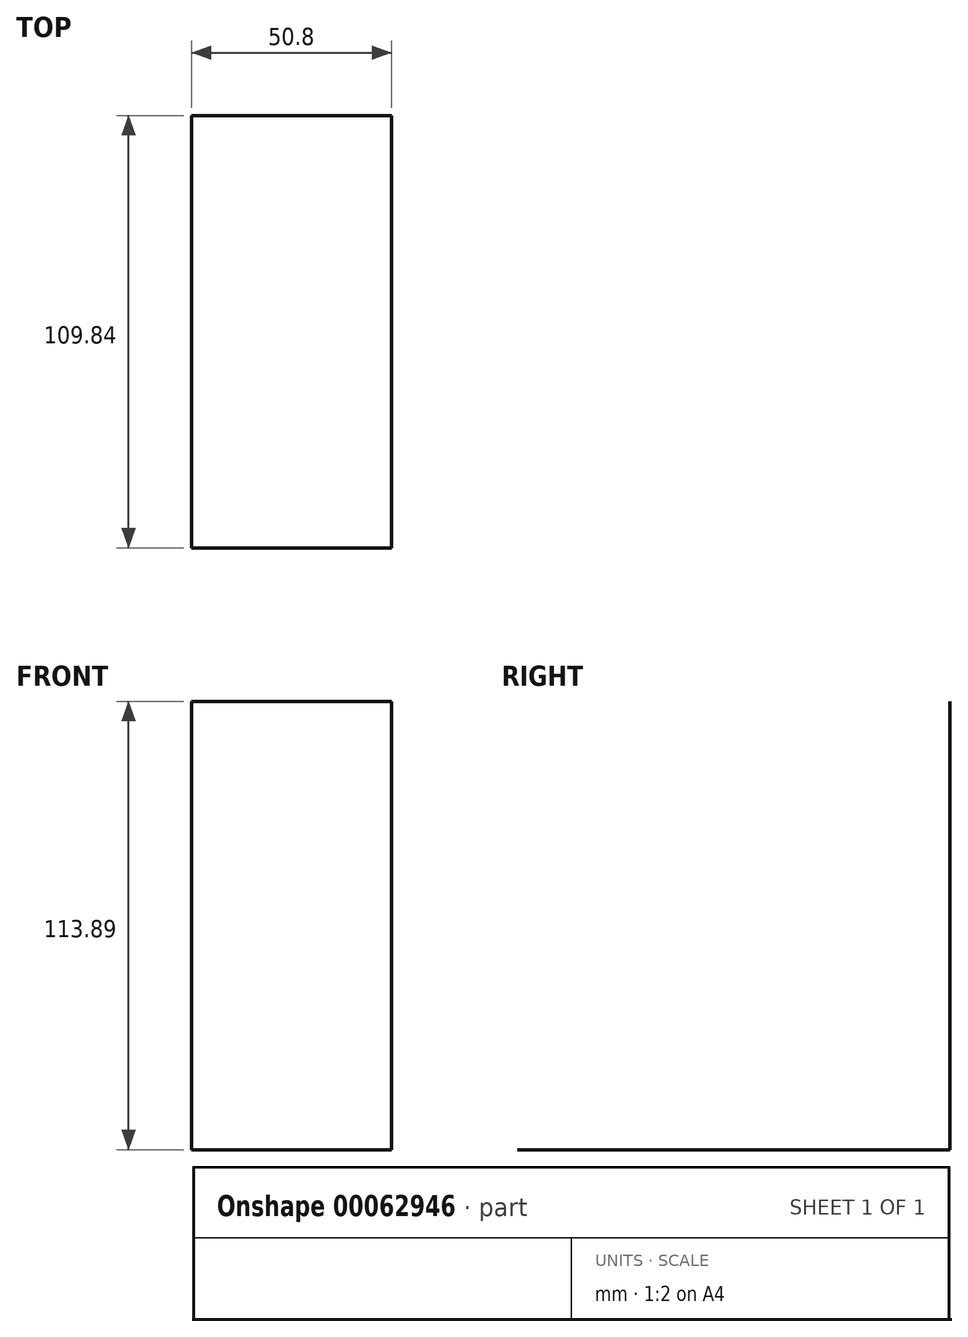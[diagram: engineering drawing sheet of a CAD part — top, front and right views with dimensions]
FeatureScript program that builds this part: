
annotation { "Feature Type Name" : "Feature", "Feature Type Description" : "" }
export const myFeature = defineFeature(function(context is Context, id is Id, definition is map)
    precondition{}
    {
        {
            var Q0;
            Q0=qCreatedBy(makeId("Right.planeOp"),FACE);
            var sketch = newSketch(context, id + "F0", { "sketchPlane" : qUnion([Q0])});
            skLineSegment(sketch, "E0.bottom", {"start": v(-59.27, -65.92) * mm, "end": v(50.57, -65.92) * mm});
            skLineSegment(sketch, "E0.top", {"start": v(-59.27, 47.97) * mm, "end": v(50.57, 47.97) * mm});
            skLineSegment(sketch, "E0.left", {"start": v(-59.27, -65.92) * mm, "end": v(-59.27, 47.97) * mm});
            skLineSegment(sketch, "E0.right", {"start": v(50.57, -65.92) * mm, "end": v(50.57, 47.97) * mm});
            skSolve(sketch);
        }
        {
            var Q0;
            Q0=sQuery(id+"F0.wireOp",EDGE,"E0.right");
            var Q1;
            Q1=sQuery(id+"F0.wireOp",EDGE,"E0.bottom");
            extrude(context, id + "F1", {"bodyType" : ToolBodyType.SURFACE, "surfaceEntities" : qUnion([Q0, Q1]), "depth" : 25.4 * mm, "hasSecondDirection" : true, "secondDirectionOppositeDirection" : true, "secondDirectionDepth" : 25.4 * mm});
        }
    });
